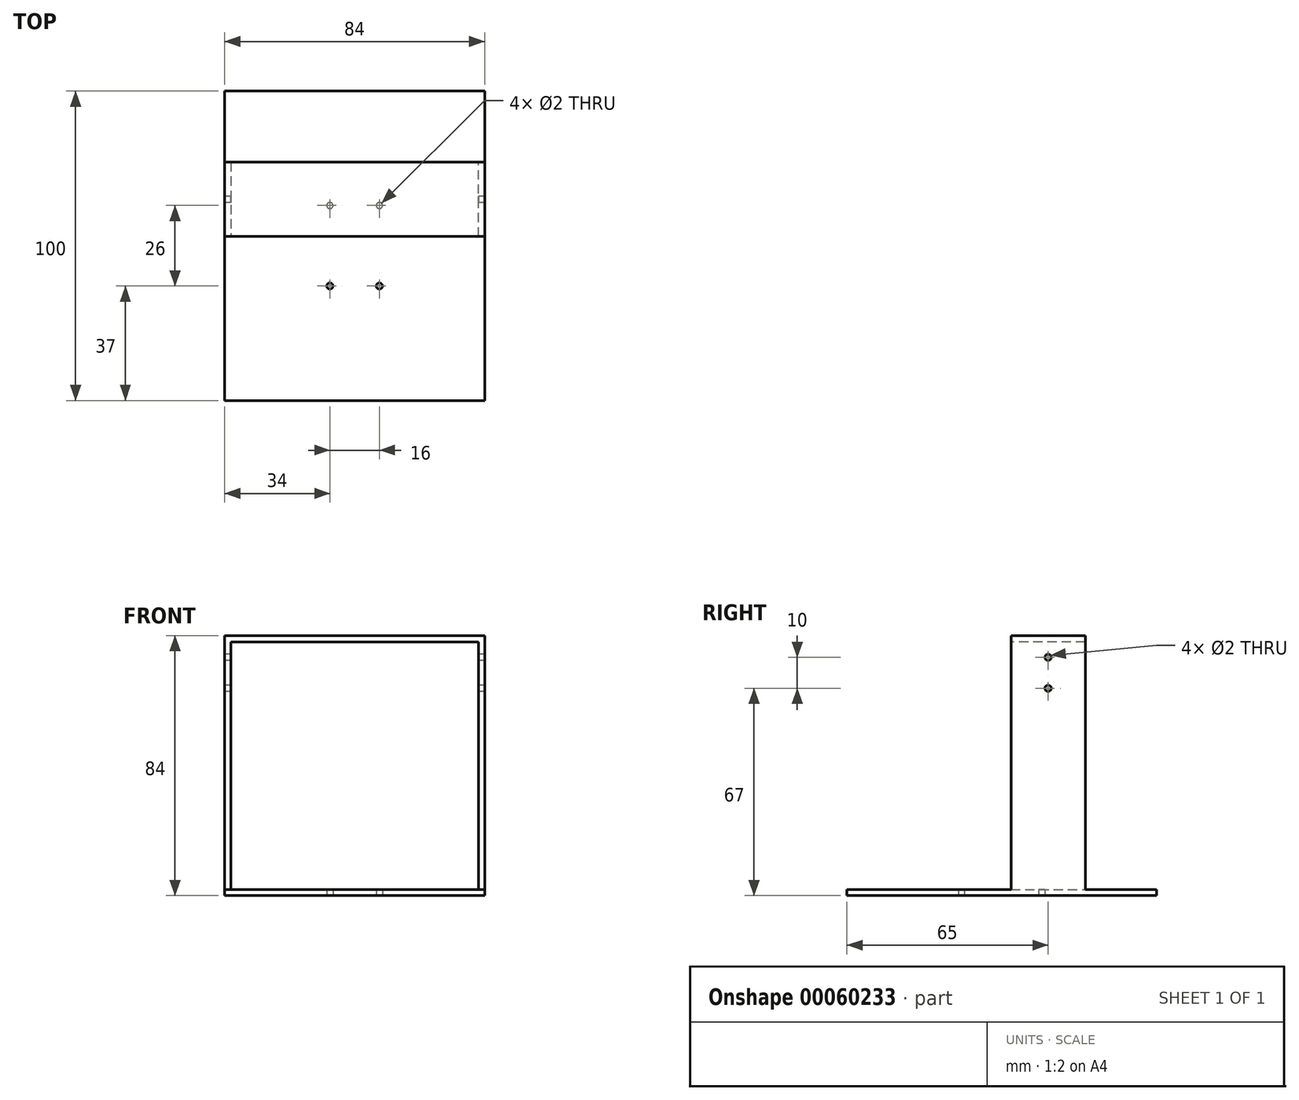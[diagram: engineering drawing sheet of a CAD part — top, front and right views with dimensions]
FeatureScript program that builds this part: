
annotation { "Feature Type Name" : "Feature", "Feature Type Description" : "" }
export const myFeature = defineFeature(function(context is Context, id is Id, definition is map)
    precondition{}
    {
        {
            var Q0;
            Q0=qCreatedBy(makeId("Top.planeOp"),FACE);
            var sketch = newSketch(context, id + "F0", { "sketchPlane" : qUnion([Q0])});
            skLineSegment(sketch, "E0.bottom", {"start": v(0, 0) * mm, "end": v(84, 0) * mm});
            skLineSegment(sketch, "E0.top", {"start": v(0, -100) * mm, "end": v(84, -100) * mm});
            skLineSegment(sketch, "E0.left", {"start": v(0, 0) * mm, "end": v(0, -100) * mm});
            skLineSegment(sketch, "E0.right", {"start": v(84, 0) * mm, "end": v(84, -100) * mm});
            skSolve(sketch);
        }
        {
            var Q0;
            Q0 = qSketchRegion(id + "F0", true);
            extrude(context, id + "F1", {"entities" : qUnion([Q0]), "depth" : 2 * mm});
        }
        {
            var Q0;
            Q0=makeQuery(id+"F1.opExtrude","CAP_FACE",FACE,{"disambiguationData":[OSD([sQuery(id+"F0.wireOp",EDGE,"E0.bottom"),sQuery(id+"F0.wireOp",EDGE,"E0.top"),sQuery(id+"F0.wireOp",EDGE,"E0.left"),sQuery(id+"F0.wireOp",EDGE,"E0.right")])],"isStart":false});
            var sketch = newSketch(context, id + "F2", { "sketchPlane" : qUnion([Q0])});
            skLineSegment(sketch, "E1.bottom", {"start": v(0, -23) * mm, "end": v(2, -23) * mm});
            skLineSegment(sketch, "E1.top", {"start": v(0, -47) * mm, "end": v(2, -47) * mm});
            skLineSegment(sketch, "E1.left", {"start": v(0, -23) * mm, "end": v(0, -47) * mm});
            skLineSegment(sketch, "E1.right", {"start": v(2, -23) * mm, "end": v(2, -47) * mm});
            skLineSegment(sketch, "E2.bottom", {"start": v(84, -47) * mm, "end": v(82, -47) * mm});
            skLineSegment(sketch, "E2.top", {"start": v(84, -23) * mm, "end": v(82, -23) * mm});
            skLineSegment(sketch, "E2.left", {"start": v(84, -47) * mm, "end": v(84, -23) * mm});
            skLineSegment(sketch, "E2.right", {"start": v(82, -47) * mm, "end": v(82, -23) * mm});
            skSolve(sketch);
        }
        {
            var Q0;
            Q0 = qSketchRegion(id + "F2", true);
            extrude(context, id + "F3", {"entities" : qUnion([Q0]), "operationType" : NewBodyOperationType.ADD, "depth" : 80 * mm});
        }
        {
            var Q0;
            Q0=makeQuery(id+"F3.opExtrude","CAP_FACE",FACE,{"disambiguationData":[OSD([sQuery(id+"F2.wireOp",EDGE,"E1.bottom"),sQuery(id+"F2.wireOp",EDGE,"E1.top"),sQuery(id+"F2.wireOp",EDGE,"E1.left"),sQuery(id+"F2.wireOp",EDGE,"E1.right")])],"isStart":false});
            var sketch = newSketch(context, id + "F4", { "sketchPlane" : qUnion([Q0])});
            skLineSegment(sketch, "E3.bottom", {"start": v(0, -23) * mm, "end": v(84, -23) * mm});
            skLineSegment(sketch, "E3.top", {"start": v(0, -47) * mm, "end": v(84, -47) * mm});
            skLineSegment(sketch, "E3.left", {"start": v(0, -23) * mm, "end": v(0, -47) * mm});
            skLineSegment(sketch, "E3.right", {"start": v(84, -23) * mm, "end": v(84, -47) * mm});
            skSolve(sketch);
        }
        {
            var Q0;
            Q0 = qSketchRegion(id + "F4", true);
            extrude(context, id + "F5", {"entities" : qUnion([Q0]), "operationType" : NewBodyOperationType.ADD, "depth" : 2 * mm});
        }
        {
            var Q0;
            Q0=makeQuery(id+"F1.opExtrude","CAP_FACE",FACE,{"disambiguationData":[OSD([sQuery(id+"F0.wireOp",EDGE,"E0.bottom"),sQuery(id+"F0.wireOp",EDGE,"E0.top"),sQuery(id+"F0.wireOp",EDGE,"E0.left"),sQuery(id+"F0.wireOp",EDGE,"E0.right")])],"isStart":false});
            var sketch = newSketch(context, id + "F6", { "sketchPlane" : qUnion([Q0])});
            skLineSegment(sketch, "E4.bottom", {"start": v(34, -37) * mm, "end": v(50, -37) * mm});
            skLineSegment(sketch, "E4.top", {"start": v(34, -63) * mm, "end": v(50, -63) * mm});
            skLineSegment(sketch, "E4.left", {"start": v(34, -37) * mm, "end": v(34, -63) * mm});
            skLineSegment(sketch, "E4.right", {"start": v(50, -37) * mm, "end": v(50, -63) * mm});
            skCircle(sketch, "E5", {"center": v(34, -37) * mm, "radius": 1 * mm});
            skCircle(sketch, "E6", {"center": v(50, -37) * mm, "radius": 1 * mm});
            skCircle(sketch, "E7", {"center": v(34, -63) * mm, "radius": 1 * mm});
            skCircle(sketch, "E8", {"center": v(50, -63) * mm, "radius": 1 * mm});
            skSolve(sketch);
        }
        {
            var Q0;
            Q0=sQuery(id+"F6.wireOp",VERTEX,"E4.left.start");
            var Q1;
            Q1=sQuery(id+"F6.wireOp",VERTEX,"E4.right.start");
            var Q2;
            Q2=sQuery(id+"F6.wireOp",VERTEX,"E4.top.end");
            var Q3;
            Q3=sQuery(id+"F6.wireOp",VERTEX,"E4.left.end");
            var Q4;
            Q4=makeQuery(id+"F1.opExtrude","SWEPT_BODY",BODY,{"disambiguationData":[OSD([sQuery(id+"F0.wireOp",EDGE,"E0.bottom"),sQuery(id+"F0.wireOp",EDGE,"E0.top"),sQuery(id+"F0.wireOp",EDGE,"E0.left"),sQuery(id+"F0.wireOp",EDGE,"E0.right")])]});
            hole(context, id + "F7", {"style" : HoleStyle.SIMPLE, "holeDiameter" : 2 * mm, "endStyle" : HoleEndStyle.THROUGH, "locations" : qUnion([Q0, Q1, Q2, Q3]), "scope" : qUnion([Q4])});
        }
        {
            var Q0;
            Q0=makeQuery(id+"F5.boolean.opBoolean","MERGE",FACE,{"derivedFrom":[makeQuery(id+"F3.boolean.opBoolean","MERGE",FACE,{"derivedFrom":[makeQuery(id+"F1.opExtrude","SWEPT_FACE",FACE,{"disambiguationData":[OSD([sQuery(id+"F0.wireOp",EDGE,"E0.right")])]}),makeQuery(id+"F3.opExtrude","SWEPT_FACE",FACE,{"disambiguationData":[OSD([sQuery(id+"F2.wireOp",EDGE,"E2.left")])]})]}),makeQuery(id+"F5.opExtrude","SWEPT_FACE",FACE,{"disambiguationData":[OSD([sQuery(id+"F4.wireOp",EDGE,"E3.right")])]})]});
            var sketch = newSketch(context, id + "F8", { "sketchPlane" : qUnion([Q0])});
            skCircle(sketch, "E9", {"center": v(-35, 77) * mm, "radius": 1 * mm});
            skCircle(sketch, "E10", {"center": v(-35, 67) * mm, "radius": 1 * mm});
            skSolve(sketch);
        }
        {
            var Q0;
            Q0=sQuery(id+"F8.wireOp",VERTEX,"E9.center");
            var Q1;
            Q1=sQuery(id+"F8.wireOp",VERTEX,"E10.center");
            var Q2;
            Q2=makeQuery(id+"F1.opExtrude","SWEPT_BODY",BODY,{"disambiguationData":[OSD([sQuery(id+"F0.wireOp",EDGE,"E0.bottom"),sQuery(id+"F0.wireOp",EDGE,"E0.top"),sQuery(id+"F0.wireOp",EDGE,"E0.left"),sQuery(id+"F0.wireOp",EDGE,"E0.right")])]});
            hole(context, id + "F9", {"style" : HoleStyle.SIMPLE, "holeDiameter" : 2 * mm, "endStyle" : HoleEndStyle.THROUGH, "locations" : qUnion([Q0, Q1]), "scope" : qUnion([Q2])});
        }
    });
